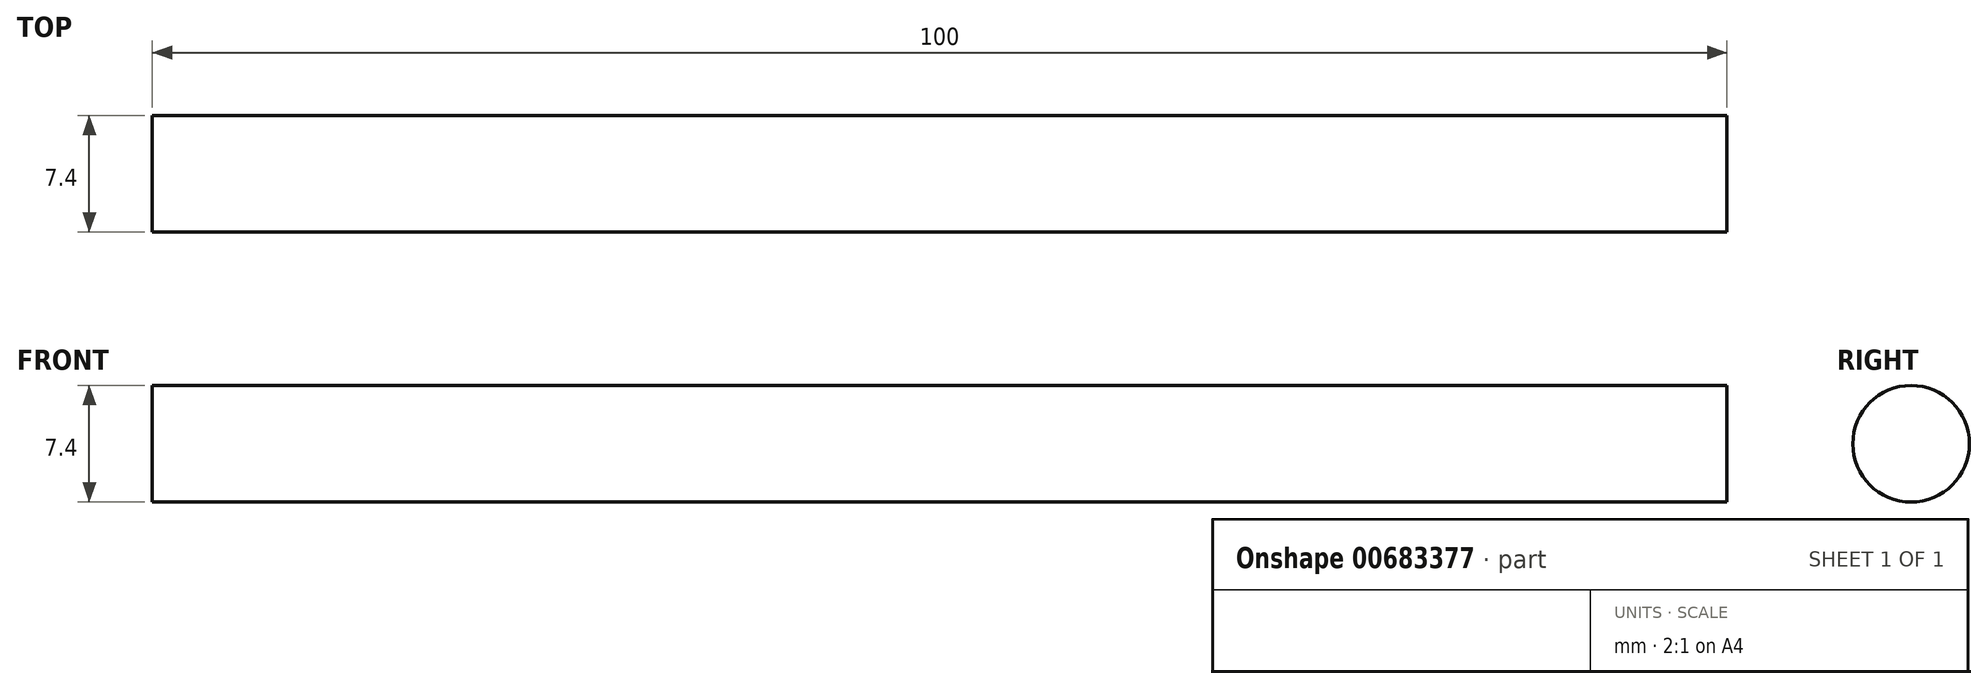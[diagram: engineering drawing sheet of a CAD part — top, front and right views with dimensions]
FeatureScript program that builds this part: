
annotation { "Feature Type Name" : "Feature", "Feature Type Description" : "" }
export const myFeature = defineFeature(function(context is Context, id is Id, definition is map)
    precondition{}
    {
        {
            var Q0;
            Q0=qCreatedBy(makeId("Top.planeOp"),FACE);
            var sketch = newSketch(context, id + "F0", { "sketchPlane" : qUnion([Q0])});
            skLineSegment(sketch, "E0", {"start": v(0, 0) * mm, "end": v(100, 0) * mm});
            skSolve(sketch);
        }
        {
            var Q0;
            Q0=qCreatedBy(makeId("Right.planeOp"),FACE);
            var sketch = newSketch(context, id + "F1", { "sketchPlane" : qUnion([Q0])});
            skCircle(sketch, "E1", {"center": v(0, 0) * mm, "radius": 3.7 * mm});
            skSolve(sketch);
        }
        {
            var Q0;
            Q0=makeQuery(id+"F1.imprint","IMPRINT",FACE,{"disambiguationData":[TD([[makeQuery(id+"F1.imprint","IMPRINT",EDGE,{"derivedFrom":sQuery(id+"F1.wireOp",EDGE,"E1")}),1.0]])]});
            var Q1;
            Q1=sQuery(id+"F0.wireOp",EDGE,"E0");
            sweep(context, id + "F2", {"profiles" : qUnion([Q0]), "path" : qUnion([Q1])});
        }
    });
